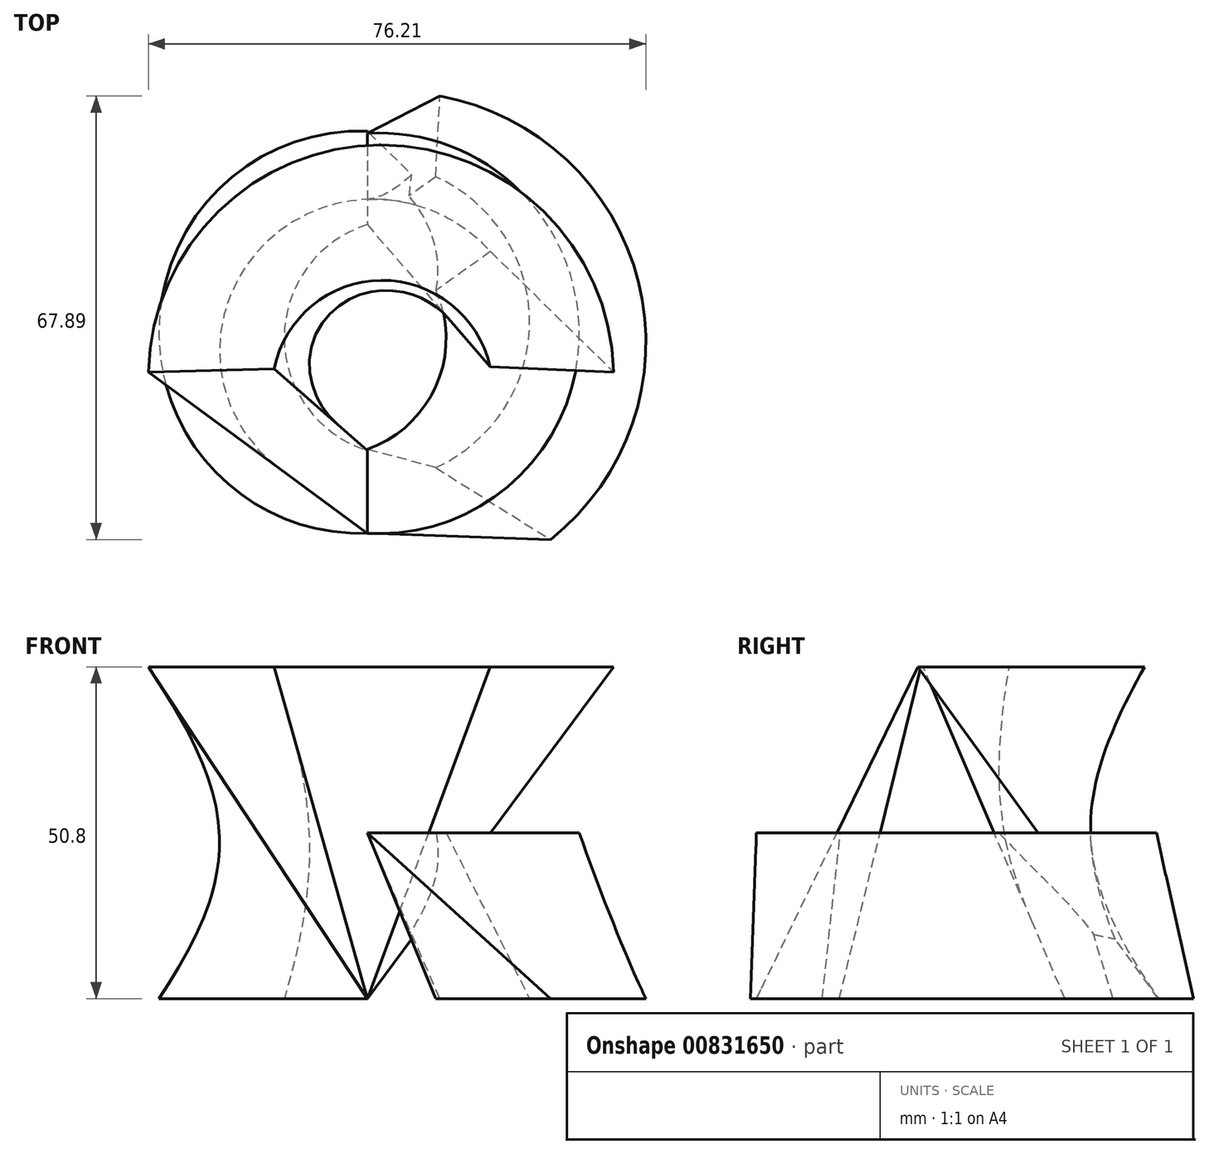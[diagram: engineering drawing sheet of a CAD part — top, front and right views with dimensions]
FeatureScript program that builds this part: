
annotation { "Feature Type Name" : "Feature", "Feature Type Description" : "" }
export const myFeature = defineFeature(function(context is Context, id is Id, definition is map)
    precondition{}
    {
        {
            var Q0;
            Q0=qCreatedBy(makeId("Top.planeOp"),FACE);
            cPlane(context, id + "F0", {"entities" : qUnion([Q0]), "cplaneType" : CPlaneType.OFFSET, "offset" : 25.4 * mm, "width" : 152.4 * mm, "height" : 152.4 * mm});
        }
        {
            var Q0;
            Q0=qCreatedBy(id+"F0.planeOp",FACE);
            cPlane(context, id + "F1", {"entities" : qUnion([Q0]), "cplaneType" : CPlaneType.OFFSET, "offset" : 25.4 * mm, "width" : 152.4 * mm, "height" : 152.4 * mm});
        }
        {
            var Q0;
            Q0=qCreatedBy(id+"F1.planeOp",FACE);
            var sketch = newSketch(context, id + "F2", { "sketchPlane" : qUnion([Q0])});
            skArc(sketch, "E0", {"start": v(37.74, 2.02) * mm, "mid": v(2.1, 36.76) * mm, "end": v(-33.54, 2.02) * mm});
            skArc(sketch, "E1", {"start": v(18.8, 2.84) * mm, "mid": v(2.13, 16.05) * mm, "end": v(-14.28, 2.51) * mm});
            skLineSegment(sketch, "E2", {"start": v(-14.28, 2.51) * mm, "end": v(-33.54, 2.02) * mm});
            skLineSegment(sketch, "E3", {"start": v(18.8, 2.84) * mm, "end": v(37.74, 2.02) * mm});
            skSolve(sketch);
        }
        {
            var Q0;
            Q0=qCreatedBy(id+"F0.planeOp",FACE);
            var sketch = newSketch(context, id + "F3", { "sketchPlane" : qUnion([Q0])});
            skArc(sketch, "E4", {"start": v(0, -22.68) * mm, "mid": v(32.47, 7.94) * mm, "end": v(0, 38.56) * mm});
            skArc(sketch, "E5", {"start": v(0, -9.84) * mm, "mid": v(12.07, 7.2) * mm, "end": v(0, 24.24) * mm});
            skLineSegment(sketch, "E6", {"start": v(0, 38.56) * mm, "end": v(0, 24.24) * mm});
            skLineSegment(sketch, "E7", {"start": v(0, -9.84) * mm, "end": v(0, -22.68) * mm});
            skSolve(sketch);
        }
        {
            var Q0;
            Q0=qCreatedBy(makeId("Top.planeOp"),FACE);
            var sketch = newSketch(context, id + "F4", { "sketchPlane" : qUnion([Q0])});
            skArc(sketch, "E8", {"start": v(0, 38.9) * mm, "mid": v(-31.9, 8.1) * mm, "end": v(0, -22.68) * mm});
            skArc(sketch, "E9", {"start": v(0, 24.57) * mm, "mid": v(-12.71, 7.28) * mm, "end": v(0, -10) * mm});
            skLineSegment(sketch, "E10", {"start": v(0, 38.9) * mm, "end": v(0, 24.57) * mm});
            skLineSegment(sketch, "E11", {"start": v(0, -10) * mm, "end": v(0, -22.68) * mm});
            skSolve(sketch);
        }
        {
            var Q0;
            Q0=makeQuery(id+"F4.imprint","IMPRINT",FACE,{"disambiguationData":[TD([[makeQuery(id+"F4.imprint","IMPRINT",EDGE,{"derivedFrom":sQuery(id+"F4.wireOp",EDGE,"E8")}),1.0]])]});
            var Q1;
            Q1=makeQuery(id+"F2.imprint","IMPRINT",FACE,{"disambiguationData":[TD([[makeQuery(id+"F2.imprint","IMPRINT",EDGE,{"derivedFrom":sQuery(id+"F2.wireOp",EDGE,"E0")}),1.0]])]});
            loft(context, id + "F5", {"sheetProfilesArray" : [{ "sheetProfileEntities" : qUnion([Q0]) }, { "sheetProfileEntities" : qUnion([Q1]) }]});
        }
        {
            var Q0;
            Q0=makeQuery(id+"F5.opLoft","CAP_FACE",FACE,{"disambiguationData":[OSD([makeQuery(id+"F4.imprint","IMPRINT",FACE,{"disambiguationData":[TD([[makeQuery(id+"F4.imprint","IMPRINT",EDGE,{"derivedFrom":sQuery(id+"F4.wireOp",EDGE,"E8")}),1.0]])]})])],"isStart":true});
            var sketch = newSketch(context, id + "F6", { "sketchPlane" : qUnion([Q0])});
            skArc(sketch, "E12", {"start": v(11.12, -44.26) * mm, "mid": v(41.53, -15.79) * mm, "end": v(28.05, 23.63) * mm});
            skArc(sketch, "E13", {"start": v(10.46, -31.93) * mm, "mid": v(24.86, -9.65) * mm, "end": v(10.46, 12.62) * mm});
            skLineSegment(sketch, "E14", {"start": v(10.46, 12.62) * mm, "end": v(28.05, 23.63) * mm});
            skLineSegment(sketch, "E15", {"start": v(10.46, -31.93) * mm, "end": v(11.12, -44.26) * mm});
            skSolve(sketch);
        }
        {
            var Q1;
            Q1=makeQuery(id+"F6.imprint","IMPRINT",FACE,{"disambiguationData":[TD([[makeQuery(id+"F6.imprint","IMPRINT",EDGE,{"derivedFrom":sQuery(id+"F6.wireOp",EDGE,"E12")}),1.0]])]});
            var Q2;
            Q2=makeQuery(id+"F3.imprint","IMPRINT",FACE,{"disambiguationData":[TD([[makeQuery(id+"F3.imprint","IMPRINT",EDGE,{"derivedFrom":sQuery(id+"F3.wireOp",EDGE,"E4")}),1.0]])]});
            loft(context, id + "F7", {"operationType" : NewBodyOperationType.ADD, "sheetProfilesArray" : [{ "sheetProfileEntities" : qUnion([Q1]) }, { "sheetProfileEntities" : qUnion([Q2]) }]});
        }
    });
